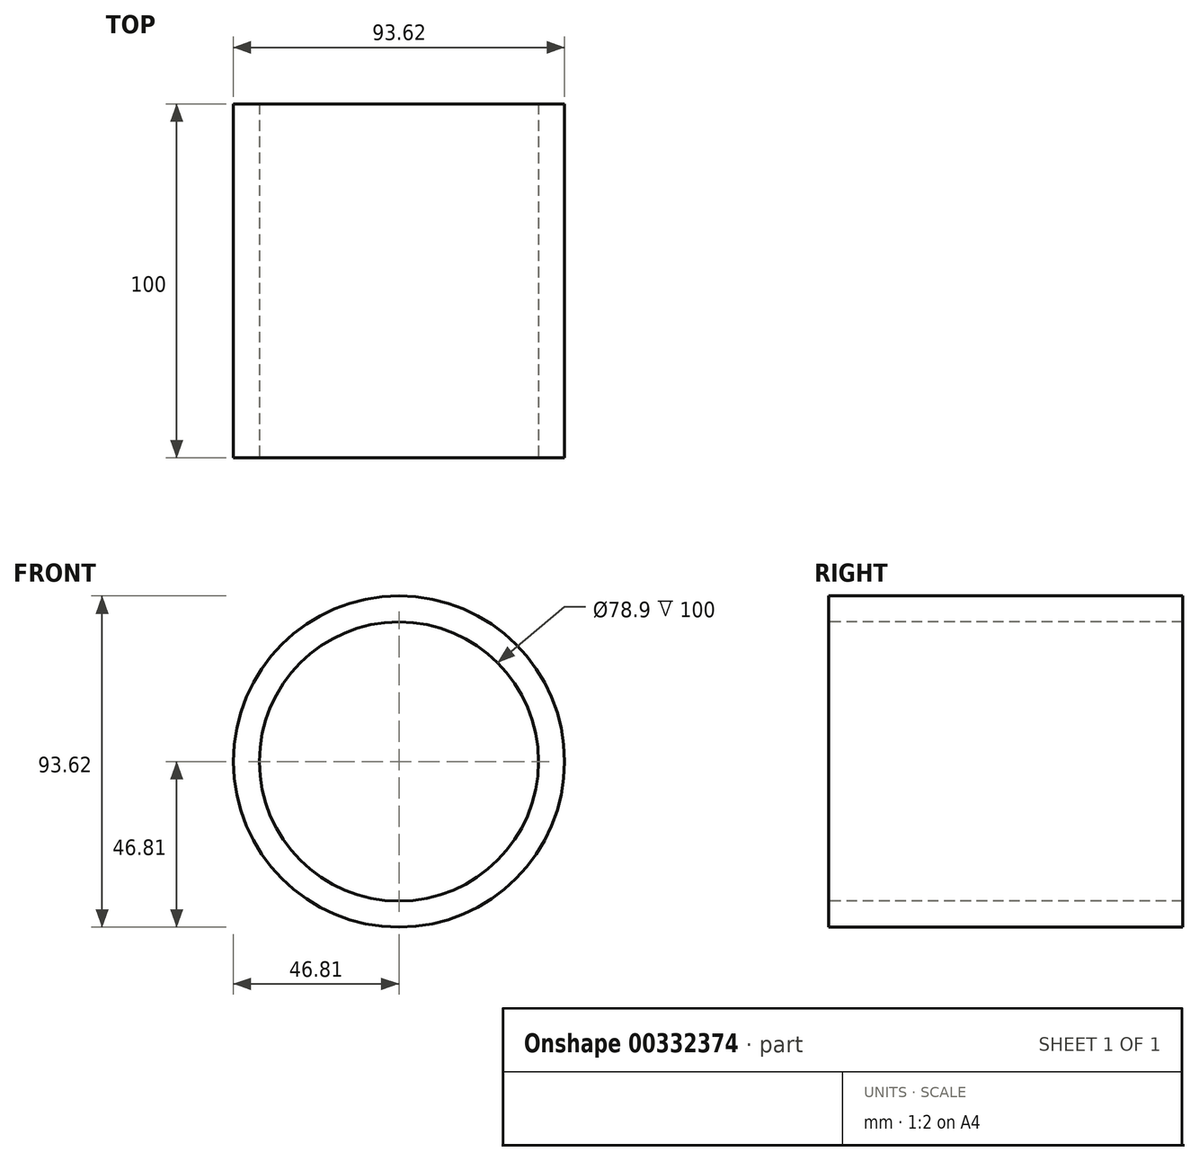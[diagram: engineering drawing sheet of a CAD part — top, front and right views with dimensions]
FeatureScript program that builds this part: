
annotation { "Feature Type Name" : "Feature", "Feature Type Description" : "" }
export const myFeature = defineFeature(function(context is Context, id is Id, definition is map)
    precondition{}
    {
        {
            var Q0;
            Q0=qCreatedBy(makeId("Front.planeOp"),FACE);
            var sketch = newSketch(context, id + "F0", { "sketchPlane" : qUnion([Q0])});
            skCircle(sketch, "E0", {"center": v(0, 0) * mm, "radius": 46.8 * mm});
            skCircle(sketch, "E1", {"center": v(0, 0) * mm, "radius": 39.45 * mm});
            skCircle(sketch, "E2", {"center": v(0, 0) * mm, "radius": 30.7 * mm});
            skCircle(sketch, "E3", {"center": v(0, 0) * mm, "radius": 21.17 * mm});
            skCircle(sketch, "E4", {"center": v(0, 0) * mm, "radius": 11.1 * mm});
            skSolve(sketch);
        }
        {
            var Q0;
            Q0=makeQuery(id+"F0.imprint","IMPRINT",FACE,{"disambiguationData":[TD([[makeQuery(id+"F0.imprint","IMPRINT",EDGE,{"derivedFrom":sQuery(id+"F0.wireOp",EDGE,"E0")}),1.0]])]});
            extrude(context, id + "F1", {"entities" : qUnion([Q0]), "oppositeDirection" : true, "depth" : 100 * mm});
        }
    });
